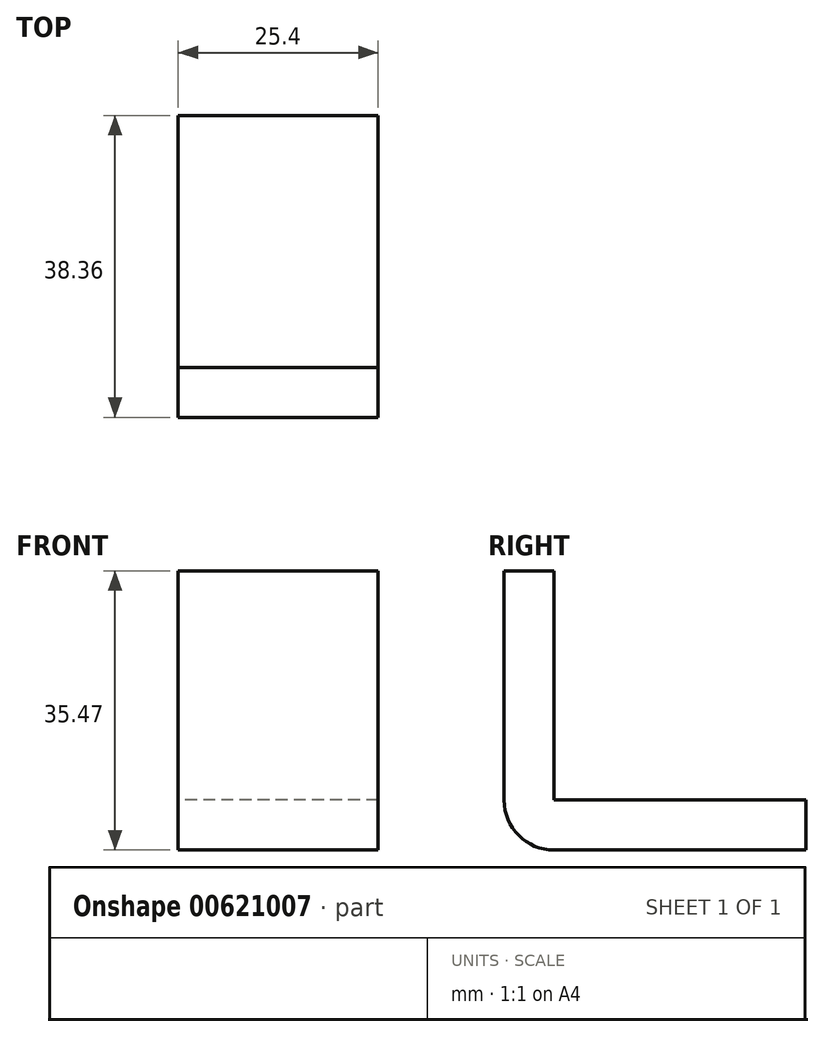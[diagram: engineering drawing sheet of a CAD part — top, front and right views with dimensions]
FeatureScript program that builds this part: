
annotation { "Feature Type Name" : "Feature", "Feature Type Description" : "" }
export const myFeature = defineFeature(function(context is Context, id is Id, definition is map)
    precondition{}
    {
        {
            var Q0;
            Q0=qCreatedBy(makeId("Right.planeOp"),FACE);
            var sketch = newSketch(context, id + "F0", { "sketchPlane" : qUnion([Q0])});
            skLineSegment(sketch, "E0", {"start": v(-37.45, 44.14) * mm, "end": v(-37.45, 15.02) * mm});
            skLineSegment(sketch, "E1", {"start": v(-37.45, 15.02) * mm, "end": v(-5.44, 15.02) * mm});
            skLineSegment(sketch, "E2.0", {"start": v(-43.8, 44.14) * mm, "end": v(-43.8, 15.02) * mm});
            skLineSegment(sketch, "E3.0", {"start": v(-37.45, 8.67) * mm, "end": v(-5.44, 8.67) * mm});
            skArc(sketch, "E4", {"start": v(-43.8, 15.02) * mm, "mid": v(-41.94, 10.53) * mm, "end": v(-37.45, 8.67) * mm});
            skLineSegment(sketch, "E5", {"start": v(-43.8, 44.14) * mm, "end": v(-37.45, 44.14) * mm});
            skLineSegment(sketch, "E6", {"start": v(-5.44, 15.02) * mm, "end": v(-5.44, 8.67) * mm});
            skSolve(sketch);
        }
        {
            var Q0;
            Q0 = qSketchRegion(id + "F0", true);
            extrude(context, id + "F1", {"entities" : qUnion([Q0]), "depth" : 25.4 * mm, "offsetDistance" : 25.4 * mm});
        }
    });
